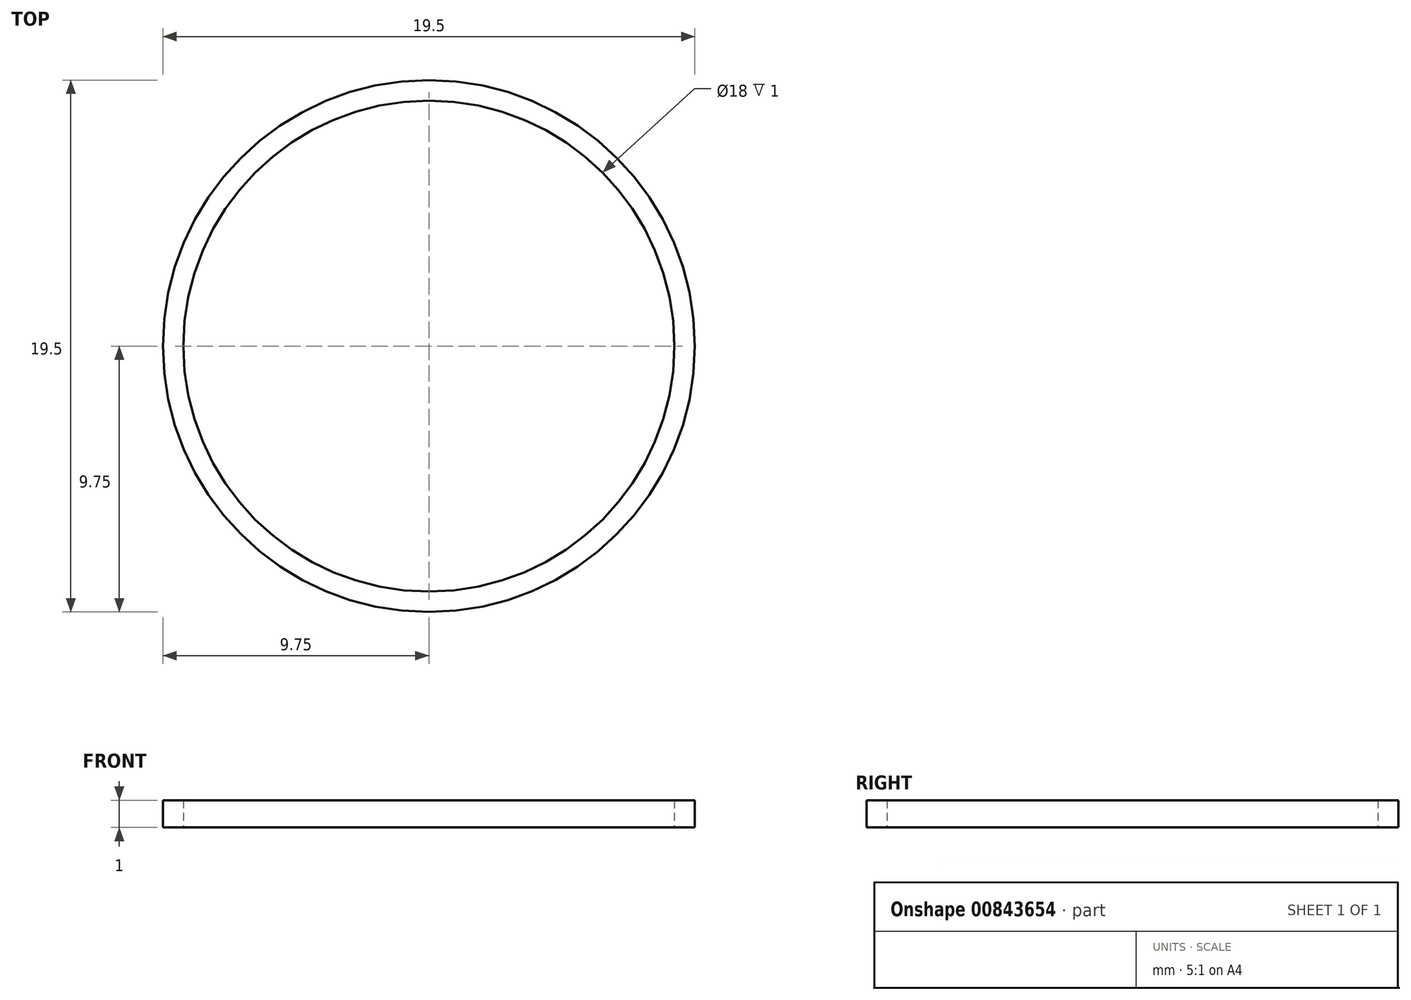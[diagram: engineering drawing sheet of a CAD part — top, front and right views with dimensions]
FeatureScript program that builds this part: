
annotation { "Feature Type Name" : "Feature", "Feature Type Description" : "" }
export const myFeature = defineFeature(function(context is Context, id is Id, definition is map)
    precondition{}
    {
        {
            var Q0;
            Q0=qCreatedBy(makeId("Top.planeOp"),FACE);
            var sketch = newSketch(context, id + "F0", { "sketchPlane" : qUnion([Q0])});
            skCircle(sketch, "E0", {"center": v(0, 0) * mm, "radius": 9 * mm});
            skCircle(sketch, "E1", {"center": v(0, 0) * mm, "radius": 9.75 * mm});
            skSolve(sketch);
        }
        {
            var Q0;
            Q0 = qSketchRegion(id + "F0", true);
            extrude(context, id + "F1", {"entities" : qUnion([Q0]), "depth" : mm, "offsetDistance" : 25.4 * mm});
        }
    });
